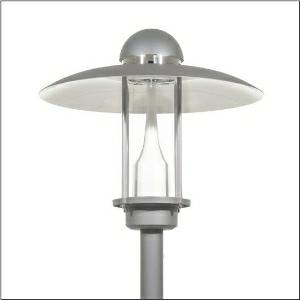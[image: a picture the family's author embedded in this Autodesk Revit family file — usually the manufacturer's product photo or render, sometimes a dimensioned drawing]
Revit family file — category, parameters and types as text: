
# Revit family: city-light_elegance_iq___st1_2a_5xa5265af14h_1cc4
name_source: partatom
category: Lighting Fixtures
units: mm (PartAtom-declared; Revit-internal decimal feet)

## family parameters
Cut with Voids When Loaded = No
Host = Face
Light Source = No
Part Type = Normal
Room Calculation Point = No
Round Connector Dimension = Use Diameter
Shared = No

## types (1)
- --- (1 x LED, 1470 lm, 12.9 W, 2200K)
    Apparent Load = 13 VA
    CIE Flux Codes = 22 62 94 98 100
    Color Rendering = 70
    Color Temperature = 2200K
    Default Elevation = 1800 mm
    Description = City-Light Elegance iQ, mast luminaire, Module 540 iQ-SR, primary light control with 3 zone facetted reflector, of plastic, silver coated, highly specular, structured, primary optical cover: cover, of PMMA, transparent, light distribution: ST1.2a, light emission: direct distribution, primary light characteristic: asymmetric, installation type: post-top, LED, High Power LED, rated luminous flux: 1.470lm, luminous efficacy: 114lm/W, light colour: 722, colour temperature: 2200K, control gear: iQ Street-Remote, control: pre-setting: logarithmic dimming characteristic, Street-Remote, Auto-Match, Temp-Guard, Lumen-Switch, Night-Set, Smart-Wire, Light-Fading, Desk-Remote (wireless, voltage-free reading and setting of iQ features in the workshop via application-optimized NFC function/RFID function), optimised constant luminous flux control (CLO 2.0), with terminal, 6-pole, max. 2.5mm², mains connection: 230..240V, AC, 50/60Hz, start of lifetime: 13W, end of service life: 13W, reduction: 6W, luminaire housing, upper part, of aluminium, coated, Siteco® metallic grey (DB 702S), diameter: 750mm, height: 675mm, spigot size: d x l = 76 x 70mm (post-top) | with reducer (optional accessory) 60 x 70mm, mounting height: 3..5m, post-top mast mounting element, of diecast aluminium, coated, Siteco® metallic grey (DB 702S), Module 540 iQ-SR, traffic white (RAL 9016), equipment: standard, protection rating (complete): IP65, insulation class (complete): insulation class II (safety insulation), certification: CE, ENEC, VDE, packaging unit: 1 piece

Light Distribution: ST1.2a
    Height = 675 mm
    Lamp = 1 x LED
    Lamp Light Flux = 1470 lm
    Lamp Power = 12.9 W
    Lamp count = 1
    Length = 750 mm
    Luminous efficacy = 114 lm/W
    Manufacturer = Siteco
    ModVariant = No
    Model = 5XA5265AF14H
    Number of Poles = 1
    OnlyDefault = Yes
    Power Factor = 1
    Product Name = City-Light Elegance iQ | ST1.2a
    Product group = mast luminaire | pylon top
    ProductGroupID = 6100
    Protection Class = Protection class II
    Protection Degree = IP 65
    RLX_Detail_Level = 1
    RLX_Emergency_Light_Flux = 0 lm
    RLX_Emergency_Type = 0
    RLX_Emergency_Type_DB = No
    RlxData = <blob elided: 61061 chars, md5=b4707494>
    Socket = socket
    Standby Power = 0 W
    System Light Flux = 1470 lm
    System Power = 13 W
    Type Comments = factory setting: luminous flux: 100 % | dim-lin: 254 | 516 mA
    Type Image = l_1006912.jpg
    URL = http://relux.com
    VarID = @adj_159912
    Voltage = 0 V
    Weight = 0.00 kg
    Width = 0 mm  [stored 0 ft]

note: [stored X ft] marks values corroborated as IEEE doubles in the binary element streams (Revit-internal decimal feet)

## geometry (parser evidence)
native form markers: Blend x4, Sweep x10
no freeform markers — native parametric forms only
